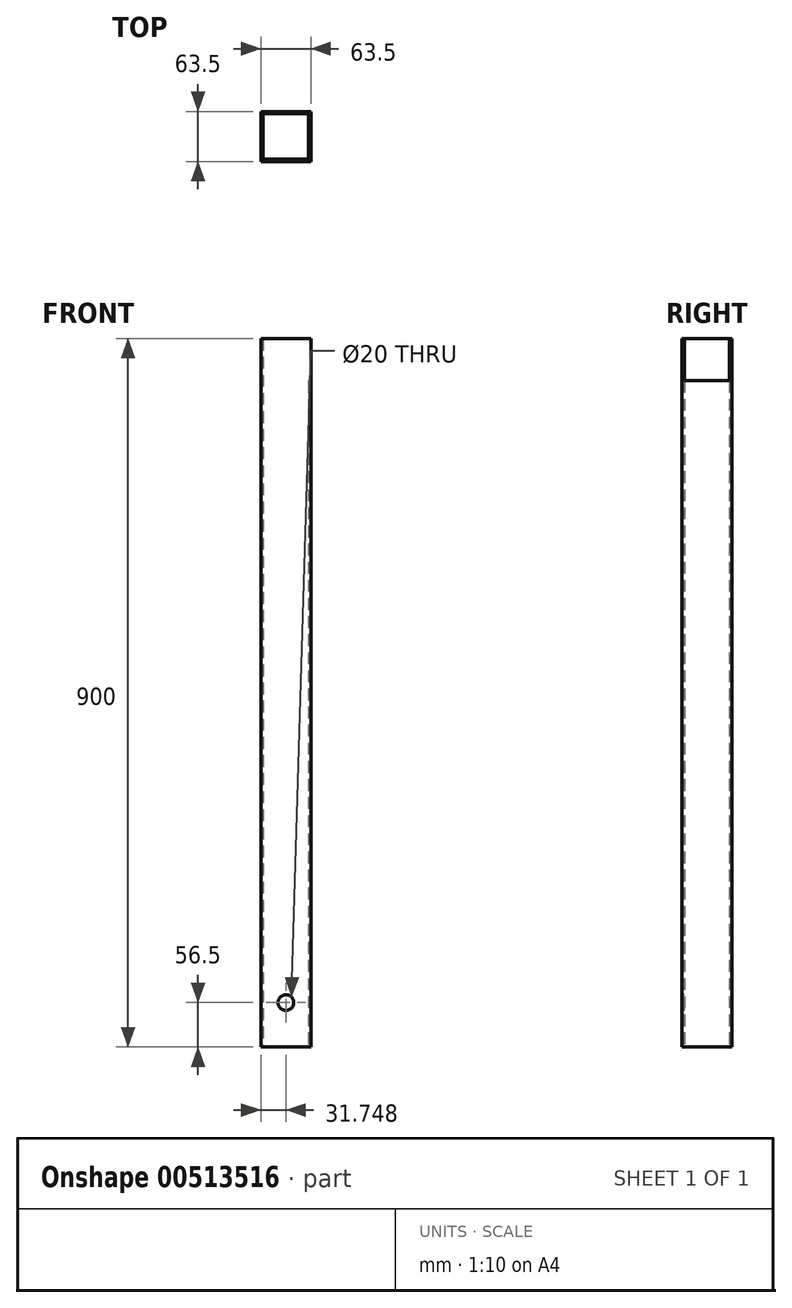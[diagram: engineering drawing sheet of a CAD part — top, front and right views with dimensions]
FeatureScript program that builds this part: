
annotation { "Feature Type Name" : "Feature", "Feature Type Description" : "" }
export const myFeature = defineFeature(function(context is Context, id is Id, definition is map)
    precondition{}
    {
        {
            var Q0;
            Q0=qCreatedBy(makeId("Top.planeOp"),FACE);
            var sketch = newSketch(context, id + "F0", { "sketchPlane" : qUnion([Q0])});
            skLineSegment(sketch, "E0.bottom", {"start": v(-27.53, 27.67) * mm, "end": v(29.97, 27.67) * mm});
            skLineSegment(sketch, "E0.top", {"start": v(-27.53, -29.83) * mm, "end": v(29.97, -29.83) * mm});
            skLineSegment(sketch, "E0.left", {"start": v(-27.53, 27.67) * mm, "end": v(-27.53, -29.83) * mm});
            skLineSegment(sketch, "E0.right", {"start": v(29.97, 27.67) * mm, "end": v(29.97, -29.83) * mm});
            skLineSegment(sketch, "E1.bottom", {"start": v(-30.53, 30.67) * mm, "end": v(32.97, 30.67) * mm});
            skLineSegment(sketch, "E1.top", {"start": v(-30.53, -32.83) * mm, "end": v(32.97, -32.83) * mm});
            skLineSegment(sketch, "E1.left", {"start": v(-30.53, 30.67) * mm, "end": v(-30.53, -32.83) * mm});
            skLineSegment(sketch, "E1.right", {"start": v(32.97, 30.67) * mm, "end": v(32.97, -32.83) * mm});
            skSolve(sketch);
        }
        {
            var Q0;
            Q0=qSketchRegion(id+"F0",true);
            extrude(context, id + "F1", {"entities" : qUnion([Q0]), "depth" : 900 * mm});
        }
        {
            var Q0;
            Q0=makeQuery(id+"F1.opExtrude","SWEPT_FACE",FACE,{"disambiguationData":[OSD([sQuery(id+"F0.wireOp",EDGE,"E1.right")])]});
            var sketch = newSketch(context, id + "F2", { "sketchPlane" : qUnion([Q0])});
            skLineSegment(sketch, "E2.bottom", {"start": v(-29.83, 900) * mm, "end": v(27.67, 900) * mm});
            skLineSegment(sketch, "E2.top", {"start": v(-29.83, 846.5) * mm, "end": v(27.67, 846.5) * mm});
            skLineSegment(sketch, "E2.left", {"start": v(-29.83, 900) * mm, "end": v(-29.83, 846.5) * mm});
            skLineSegment(sketch, "E2.right", {"start": v(27.67, 900) * mm, "end": v(27.67, 846.5) * mm});
            skSolve(sketch);
        }
        {
            var Q0;
            Q0=qSketchRegion(id+"F2",true);
            extrude(context, id + "F3", {"entities" : qUnion([Q0]), "operationType" : NewBodyOperationType.REMOVE, "oppositeDirection" : true, "offsetDistance" : 25 * mm, "depth" : 4 * mm});
        }
        {
            var Q0;
            Q0=makeQuery(id+"F1.opExtrude","SWEPT_FACE",FACE,{"disambiguationData":[OSD([sQuery(id+"F0.wireOp",EDGE,"E1.top")])]});
            var sketch = newSketch(context, id + "F4", { "sketchPlane" : qUnion([Q0])});
            skCircle(sketch, "E3", {"center": v(1.22, 56.5) * mm, "radius": 10 * mm});
            skSolve(sketch);
        }
        {
            var Q0;
            Q0 = qSketchRegion(id + "F4", true);
            extrude(context, id + "F5", {"entities" : qUnion([Q0]), "operationType" : NewBodyOperationType.REMOVE, "flatOperationType" : FlatOperationType.REMOVE, "oppositeDirection" : true, "depth" : 3 * mm, "offsetDistance" : 25 * mm, "domain" : OperationDomain.MODEL});
        }
    });
